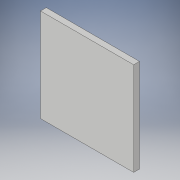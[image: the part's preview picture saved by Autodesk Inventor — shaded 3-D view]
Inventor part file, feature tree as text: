
AUTODESK INVENTOR PART (.ipt)
format: ipt  version: 2019 (Build 230136000, 136)  size: 87,040 bytes
history: native  units: in
note: dims shown in document units (in); Inventor stores cm internally (conversion verified against a paired STEP export)
features: extrude x1, sketch x1
ambient origin geometry x8: Origin, YZ Plane, XZ Plane, XY Plane, X Axis, Y Axis, Z Axis, Center Point
bodies: Solid1 (feature_tree)
feature tree (2):
  extrude  "Extrusion1"  Depth=0.0197in TaperAngle=0.0deg
  sketch  "Sketch1"  dims[d0=0.315in d1=0.0197in d2=0.0in]
